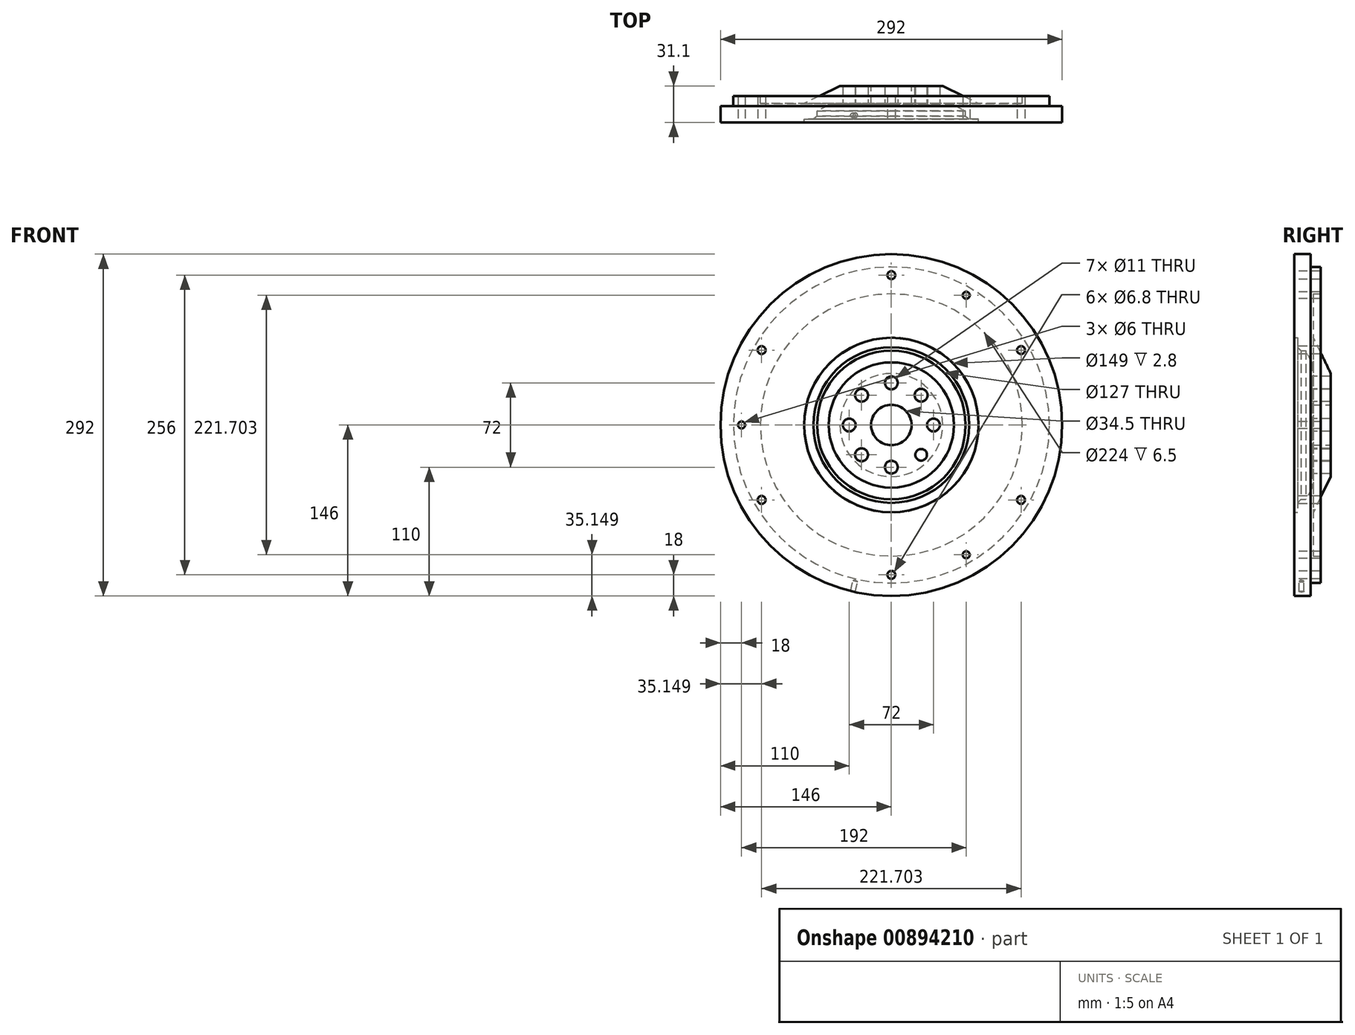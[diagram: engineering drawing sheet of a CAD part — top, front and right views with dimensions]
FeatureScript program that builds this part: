
annotation { "Feature Type Name" : "Feature", "Feature Type Description" : "" }
export const myFeature = defineFeature(function(context is Context, id is Id, definition is map)
    precondition{}
    {
        {
            var Q0;
            Q0=qCreatedBy(makeId("Right.planeOp"),FACE);
            var sketch = newSketch(context, id + "F0", { "sketchPlane" : qUnion([Q0])});
            skLineSegment(sketch, "E0.MirrorCS", {"start": v(-31.1, 74.5) * mm, "end": v(-28.3, 74.5) * mm});
            skLineSegment(sketch, "E1.MirrorCS", {"start": v(-31.1, 146) * mm, "end": v(-17.1, 146) * mm});
            skLineSegment(sketch, "E2.MirrorCS", {"start": v(-15, 112) * mm, "end": v(-8.5, 112) * mm});
            skLineSegment(sketch, "E3.MirrorCS", {"start": v(-25.6, 63.5) * mm, "end": v(-21.3, 63.5) * mm});
            skLineSegment(sketch, "E4.MirrorCS", {"start": v(-28.3, 74.5) * mm, "end": v(-28.3, 66.5) * mm});
            skLineSegment(sketch, "E5.MirrorCS", {"start": v(0, 17.25) * mm, "end": v(-16.1, 17.25) * mm});
            skLineSegment(sketch, "E6.MirrorCS", {"start": v(-8.5, 135) * mm, "end": v(-17.1, 135) * mm});
            skLineSegment(sketch, "E7.MirrorCS", {"start": v(-25.6, 63.5) * mm, "end": v(-28.3, 66.5) * mm});
            skLineSegment(sketch, "E8.MirrorCS", {"start": v(-16.1, 53.5) * mm, "end": v(-21.3, 63.5) * mm});
            skLineSegment(sketch, "E9.MirrorCS", {"start": v(-17.1, 135) * mm, "end": v(-17.1, 146) * mm});
            skLineSegment(sketch, "E10.MirrorCS", {"start": v(0, 0) * mm, "end": v(-16.1, 0) * mm});
            skLineSegment(sketch, "E11.MirrorCS", {"start": v(-16.1, 53.5) * mm, "end": v(-16.1, 17.25) * mm});
            skLineSegment(sketch, "E12.MirrorCS", {"start": v(-8.5, 135) * mm, "end": v(-8.5, 112) * mm});
            skLineSegment(sketch, "E13.MirrorCS", {"start": v(0, 0) * mm, "end": v(0, 17.25) * mm, "construction": true});
            skLineSegment(sketch, "E14.MirrorCS", {"start": v(-15, 75) * mm, "end": v(-15, 112) * mm});
            skLineSegment(sketch, "E15.MirrorCS", {"start": v(0, 44) * mm, "end": v(-15, 75) * mm});
            skLineSegment(sketch, "E16.MirrorCS", {"start": v(-31.1, 74.5) * mm, "end": v(-31.1, 146) * mm});
            skLineSegment(sketch, "E17.MirrorCS", {"start": v(0, 44) * mm, "end": v(0, 17.25) * mm});
            skSolve(sketch);
        }
        {
            var Q0;
            Q0=makeQuery(id+"F0.imprint","IMPRINT",FACE,{"disambiguationData":[TD([[makeQuery(id+"F0.imprint","IMPRINT",EDGE,{"derivedFrom":sQuery(id+"F0.wireOp",EDGE,"E0.MirrorCS")}),1.0]])]});
            var Q1;
            Q1=sQuery(id+"F0.wireOp",EDGE,"E10.MirrorCS");
            revolve(context, id + "F1", {"surfaceOperationType" : NewSurfaceOperationType.NEW, "entities" : qUnion([Q0]), "axis" : qUnion([Q1]), "revolveType" : RevolveType.FULL});
        }
        {
            var Q0;
            Q0=makeQuery(id+"F1.opRevolve","SWEPT_FACE",FACE,{"disambiguationData":[OSD([sQuery(id+"F0.wireOp",EDGE,"E11.MirrorCS")])]});
            var sketch = newSketch(context, id + "F2", { "sketchPlane" : qUnion([Q0])});
            skCircle(sketch, "E18", {"center": v(0, 0) * mm, "radius": 36 * mm, "construction": true});
            skCircle(sketch, "E19", {"center": v(0, 36) * mm, "radius": 5.5 * mm});
            skCircle(sketch, "E20.1.0", {"center": v(-25.46, 25.46) * mm, "radius": 5.5 * mm});
            skCircle(sketch, "E20.2.0", {"center": v(-36, 0) * mm, "radius": 5.5 * mm});
            skCircle(sketch, "E20.3.0", {"center": v(-25.46, -25.46) * mm, "radius": 5.5 * mm});
            skCircle(sketch, "E20.4.0", {"center": v(0, -36) * mm, "radius": 5.5 * mm});
            skCircle(sketch, "E20.5.0", {"center": v(25.46, -25.46) * mm, "radius": 5 * mm});
            skCircle(sketch, "E20.6.0", {"center": v(36, 0) * mm, "radius": 5.5 * mm});
            skCircle(sketch, "E20.7.0", {"center": v(25.46, 25.46) * mm, "radius": 5.5 * mm});
            skLineSegment(sketch, "E21", {"start": v(0, 36) * mm, "end": v(0, 0) * mm, "construction": true});
            skLineSegment(sketch, "E22", {"start": v(-25.46, 25.46) * mm, "end": v(0, 0) * mm, "construction": true});
            skLineSegment(sketch, "E23", {"start": v(-36, 0) * mm, "end": v(0, 0) * mm, "construction": true});
            skLineSegment(sketch, "E24", {"start": v(-25.46, -25.46) * mm, "end": v(0, 0) * mm, "construction": true});
            skLineSegment(sketch, "E25", {"start": v(0, -36) * mm, "end": v(0, 0) * mm, "construction": true});
            skLineSegment(sketch, "E26", {"start": v(25.46, -25.46) * mm, "end": v(0, 0) * mm, "construction": true});
            skLineSegment(sketch, "E27", {"start": v(36, 0) * mm, "end": v(0, 0) * mm, "construction": true});
            skLineSegment(sketch, "E28", {"start": v(25.46, 25.46) * mm, "end": v(0, 0) * mm, "construction": true});
            skSolve(sketch);
        }
        {
            var Q0;
            Q0 = qSketchRegion(id + "F2", true);
            extrude(context, id + "F3", {"entities" : qUnion([Q0]), "operationType" : NewBodyOperationType.REMOVE, "endBound" : BoundingType.THROUGH_ALL, "oppositeDirection" : true, "depth" : 25 * mm, "offsetDistance" : 25 * mm});
        }
        {
            var Q0;
            Q0=makeQuery(id+"F1.opRevolve","SWEPT_FACE",FACE,{"disambiguationData":[OSD([sQuery(id+"F0.wireOp",EDGE,"E16.MirrorCS")])]});
            var sketch = newSketch(context, id + "F4", { "sketchPlane" : qUnion([Q0])});
            skCircle(sketch, "E29", {"center": v(0, 0) * mm, "radius": 128 * mm, "construction": true});
            skCircle(sketch, "E30", {"center": v(0, 128) * mm, "radius": 3.4 * mm});
            skCircle(sketch, "E31.1.0", {"center": v(-110.85, 64) * mm, "radius": 3.4 * mm});
            skCircle(sketch, "E31.2.0", {"center": v(-110.85, -64) * mm, "radius": 3.4 * mm});
            skCircle(sketch, "E31.3.0", {"center": v(0, -128) * mm, "radius": 3.4 * mm});
            skCircle(sketch, "E31.4.0", {"center": v(110.85, -64) * mm, "radius": 3.4 * mm});
            skCircle(sketch, "E31.5.0", {"center": v(110.85, 64) * mm, "radius": 3.4 * mm});
            skCircle(sketch, "E32", {"center": v(-128, 0) * mm, "radius": 3 * mm});
            skCircle(sketch, "E33.1.0", {"center": v(64, -110.85) * mm, "radius": 3 * mm});
            skCircle(sketch, "E33.2.0", {"center": v(64, 110.85) * mm, "radius": 3 * mm});
            skLineSegment(sketch, "E34", {"start": v(0, 0) * mm, "end": v(-128, 0) * mm, "construction": true});
            skLineSegment(sketch, "E35", {"start": v(0, 0) * mm, "end": v(0, 128) * mm, "construction": true});
            skLineSegment(sketch, "E36", {"start": v(0, 0) * mm, "end": v(-110.85, 64) * mm, "construction": true});
            skLineSegment(sketch, "E37", {"start": v(0, 0) * mm, "end": v(64, 110.85) * mm, "construction": true});
            skLineSegment(sketch, "E38", {"start": v(0, 0) * mm, "end": v(110.85, 64) * mm, "construction": true});
            skLineSegment(sketch, "E39", {"start": v(0, 0) * mm, "end": v(110.85, -64) * mm, "construction": true});
            skLineSegment(sketch, "E40", {"start": v(0, 0) * mm, "end": v(64, -110.85) * mm, "construction": true});
            skLineSegment(sketch, "E41", {"start": v(0, 0) * mm, "end": v(0, -128) * mm, "construction": true});
            skLineSegment(sketch, "E42", {"start": v(0, 0) * mm, "end": v(-110.85, -64) * mm, "construction": true});
            skSolve(sketch);
        }
        {
            var Q0;
            Q0 = qSketchRegion(id + "F4", true);
            extrude(context, id + "F5", {"entities" : qUnion([Q0]), "operationType" : NewBodyOperationType.REMOVE, "endBound" : BoundingType.THROUGH_ALL, "oppositeDirection" : true, "depth" : 25 * mm, "offsetDistance" : 25 * mm});
        }
        {
            var Q0;
            Q0=qCreatedBy(makeId("Right.planeOp"),FACE);
            var sketch = newSketch(context, id + "F6", { "sketchPlane" : qUnion([Q0])});
            skLineSegment(sketch, "E43", {"start": v(0, 0) * mm, "end": v(-100, 0) * mm});
            skSolve(sketch);
        }
        {
            var Q0;
            Q0=sQuery(id+"F6.wireOp",EDGE,"E43");
            cPlane(context, id + "F7", {"entities" : qUnion([Q0]), "cplaneType" : CPlaneType.LINE_ANGLE, "offset" : 25 * mm, "angle" : 13 * degree, "oppositeDirection" : true, "width" : 150 * mm, "height" : 150 * mm});
        }
        {
            var Q0;
            Q0=qCreatedBy(id+"F7.planeOp",FACE);
            cPlane(context, id + "F8", {"entities" : qUnion([Q0]), "cplaneType" : CPlaneType.OFFSET, "offset" : 146 * mm, "width" : 150 * mm, "height" : 150 * mm});
        }
        {
            var Q0;
            Q0=qCreatedBy(id+"F8.planeOp",FACE);
            var sketch = newSketch(context, id + "F9", { "sketchPlane" : qUnion([Q0])});
            skCircle(sketch, "E44", {"center": v(0, 25) * mm, "radius": 2 * mm});
            skSolve(sketch);
        }
        {
            var Q0;
            Q0=sQuery(id+"F9.wireOp",VERTEX,"E44.center");
            var Q1;
            Q1=makeQuery(id+"F1.opRevolve","SWEPT_BODY",BODY,{"disambiguationData":[OSD([sQuery(id+"F0.wireOp",EDGE,"E0.MirrorCS"),sQuery(id+"F0.wireOp",EDGE,"E1.MirrorCS"),sQuery(id+"F0.wireOp",EDGE,"E2.MirrorCS"),sQuery(id+"F0.wireOp",EDGE,"E3.MirrorCS"),sQuery(id+"F0.wireOp",EDGE,"E4.MirrorCS"),sQuery(id+"F0.wireOp",EDGE,"E5.MirrorCS"),sQuery(id+"F0.wireOp",EDGE,"E6.MirrorCS"),sQuery(id+"F0.wireOp",EDGE,"E7.MirrorCS"),sQuery(id+"F0.wireOp",EDGE,"E8.MirrorCS"),sQuery(id+"F0.wireOp",EDGE,"E9.MirrorCS"),sQuery(id+"F0.wireOp",EDGE,"E11.MirrorCS"),sQuery(id+"F0.wireOp",EDGE,"E12.MirrorCS"),sQuery(id+"F0.wireOp",EDGE,"E14.MirrorCS"),sQuery(id+"F0.wireOp",EDGE,"E15.MirrorCS"),sQuery(id+"F0.wireOp",EDGE,"E16.MirrorCS"),sQuery(id+"F0.wireOp",EDGE,"E17.MirrorCS")])]});
            hole(context, id + "F10", {"style" : HoleStyle.SIMPLE, "endStyle" : HoleEndStyle.BLIND, "holeDiameter" : 4 * mm, "majorDiameter" : 5 * mm, "holeDepth" : 9 * mm, "isTappedThrough" : true, "tappedDepth" : 12 * mm, "tapClearance" : 3, "locations" : qUnion([Q0]), "scope" : qUnion([Q1]), "startStyle" : HoleStartStyle.SKETCH});
        }
    });
